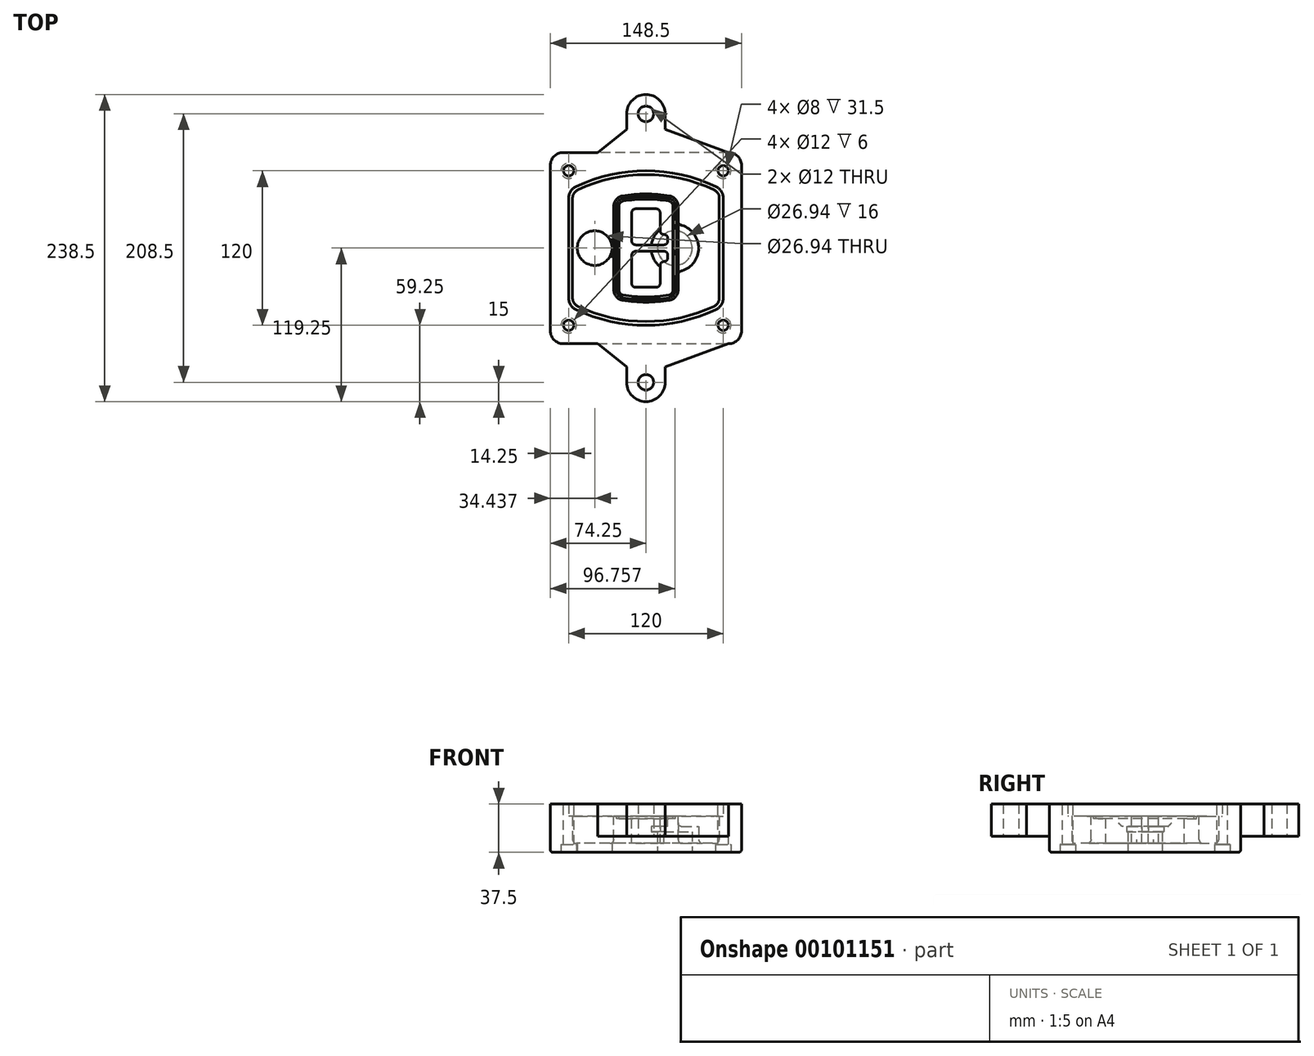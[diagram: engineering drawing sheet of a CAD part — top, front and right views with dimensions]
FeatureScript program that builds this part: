
annotation { "Feature Type Name" : "Feature", "Feature Type Description" : "" }
export const myFeature = defineFeature(function(context is Context, id is Id, definition is map)
    precondition{}
    {
        {
            var Q0;
            Q0=qCreatedBy(makeId("Top.planeOp"),FACE);
            var sketch = newSketch(context, id + "F0", { "sketchPlane" : qUnion([Q0])});
            skPoint(sketch, "E0.rect.middle", {"position": v(0, 0) * mm});
            skLineSegment(sketch, "E1.bottom", {"start": v(-64.25, -74.25) * mm, "end": v(64.25, -74.25) * mm});
            skLineSegment(sketch, "E1.top", {"start": v(-64.25, 74.25) * mm, "end": v(64.25, 74.25) * mm});
            skLineSegment(sketch, "E1.left", {"start": v(-74.25, -64.25) * mm, "end": v(-74.25, 64.25) * mm});
            skLineSegment(sketch, "E1.right", {"start": v(74.25, -64.25) * mm, "end": v(74.25, 64.25) * mm});
            skLineSegment(sketch, "E2", {"start": v(-74.25, 74.25) * mm, "end": v(74.25, -74.25) * mm, "construction": true});
            skLineSegment(sketch, "E3", {"start": v(74.25, 74.25) * mm, "end": v(-74.25, -74.25) * mm, "construction": true});
            skCircle(sketch, "E4", {"center": v(-60, 60) * mm, "radius": 4 * mm});
            skCircle(sketch, "E5", {"center": v(60, 60) * mm, "radius": 4 * mm});
            skCircle(sketch, "E6", {"center": v(60, -60) * mm, "radius": 4 * mm});
            skCircle(sketch, "E7", {"center": v(-60, -60) * mm, "radius": 4 * mm});
            skLineSegment(sketch, "E8", {"start": v(-60, 60) * mm, "end": v(60, 60) * mm, "construction": true});
            skLineSegment(sketch, "E9", {"start": v(60, 60) * mm, "end": v(60, -60) * mm, "construction": true});
            skLineSegment(sketch, "E10", {"start": v(60, -60) * mm, "end": v(-60, -60) * mm, "construction": true});
            skLineSegment(sketch, "E11", {"start": v(-60, -60) * mm, "end": v(-60, 60) * mm, "construction": true});
            skLineSegment(sketch, "E12", {"start": v(-60, 38.83) * mm, "end": v(-60, -38.83) * mm});
            skLineSegment(sketch, "E13", {"start": v(60, 38.83) * mm, "end": v(60, -38.83) * mm});
            skArc(sketch, "E14", {"start": v(54.26, 47.88) * mm, "mid": v(0, 60) * mm, "end": v(-54.26, 47.88) * mm});
            skArc(sketch, "E15", {"start": v(-54.26, -47.88) * mm, "mid": v(0, -60) * mm, "end": v(54.26, -47.88) * mm});
            skLineSegment(sketch, "E16", {"start": v(-60, 0) * mm, "end": v(60, 0) * mm, "construction": true});
            skPoint(sketch, "E17.visualSharp", {"position": v(-60, -45) * mm});
            skArc(sketch, "E17.filletArc", {"start": v(-60, -38.83) * mm, "mid": v(-58.44, -44.2) * mm, "end": v(-54.26, -47.88) * mm});
            skPoint(sketch, "E18.visualSharp", {"position": v(-60, 45) * mm});
            skArc(sketch, "E18.filletArc", {"start": v(-54.26, 47.88) * mm, "mid": v(-58.44, 44.2) * mm, "end": v(-60, 38.83) * mm});
            skPoint(sketch, "E19.visualSharp", {"position": v(60, 45) * mm});
            skArc(sketch, "E19.filletArc", {"start": v(60, 38.83) * mm, "mid": v(58.44, 44.2) * mm, "end": v(54.26, 47.88) * mm});
            skPoint(sketch, "E20.visualSharp", {"position": v(60, -45) * mm});
            skArc(sketch, "E20.filletArc", {"start": v(54.26, -47.88) * mm, "mid": v(58.44, -44.2) * mm, "end": v(60, -38.83) * mm});
            skPoint(sketch, "E21.visualSharp", {"position": v(-74.25, 74.25) * mm});
            skArc(sketch, "E21.filletArc", {"start": v(-64.25, 74.25) * mm, "mid": v(-71.32, 71.32) * mm, "end": v(-74.25, 64.25) * mm});
            skPoint(sketch, "E22.visualSharp", {"position": v(74.25, 74.25) * mm});
            skArc(sketch, "E22.filletArc", {"start": v(74.25, 64.25) * mm, "mid": v(71.32, 71.32) * mm, "end": v(64.25, 74.25) * mm});
            skPoint(sketch, "E23.visualSharp", {"position": v(74.25, -74.25) * mm});
            skArc(sketch, "E23.filletArc", {"start": v(64.25, -74.25) * mm, "mid": v(71.32, -71.32) * mm, "end": v(74.25, -64.25) * mm});
            skPoint(sketch, "E24.visualSharp", {"position": v(-74.25, -74.25) * mm});
            skArc(sketch, "E24.filletArc", {"start": v(-74.25, -64.25) * mm, "mid": v(-71.32, -71.32) * mm, "end": v(-64.25, -74.25) * mm});
            skArc(sketch, "E25.0", {"start": v(57, 38.83) * mm, "mid": v(55.9, 42.58) * mm, "end": v(52.98, 45.17) * mm});
            skLineSegment(sketch, "E25.1", {"start": v(57, 38.83) * mm, "end": v(57, -38.83) * mm});
            skArc(sketch, "E25.2", {"start": v(52.98, -45.17) * mm, "mid": v(55.9, -42.58) * mm, "end": v(57, -38.83) * mm});
            skArc(sketch, "E25.3", {"start": v(-52.98, -45.17) * mm, "mid": v(0, -57) * mm, "end": v(52.98, -45.17) * mm});
            skArc(sketch, "E25.4", {"start": v(-57, -38.83) * mm, "mid": v(-55.9, -42.58) * mm, "end": v(-52.98, -45.17) * mm});
            skArc(sketch, "E25.5", {"start": v(52.98, 45.17) * mm, "mid": v(0, 57) * mm, "end": v(-52.98, 45.17) * mm});
            skLineSegment(sketch, "E25.6", {"start": v(-57, 38.83) * mm, "end": v(-57, -38.83) * mm});
            skArc(sketch, "E25.7", {"start": v(-52.98, 45.17) * mm, "mid": v(-55.9, 42.58) * mm, "end": v(-57, 38.83) * mm});
            skArc(sketch, "E26.0", {"start": v(-55.96, 51.5) * mm, "mid": v(-61.82, 46.33) * mm, "end": v(-64, 38.83) * mm});
            skArc(sketch, "E26.1", {"start": v(55.96, 51.5) * mm, "mid": v(0, 64) * mm, "end": v(-55.96, 51.5) * mm});
            skArc(sketch, "E26.2", {"start": v(64, 38.83) * mm, "mid": v(61.82, 46.33) * mm, "end": v(55.96, 51.5) * mm});
            skLineSegment(sketch, "E26.3", {"start": v(64, 38.83) * mm, "end": v(64, -38.83) * mm});
            skArc(sketch, "E26.4", {"start": v(55.96, -51.5) * mm, "mid": v(61.82, -46.33) * mm, "end": v(64, -38.83) * mm});
            skLineSegment(sketch, "E26.5", {"start": v(-64, 38.83) * mm, "end": v(-64, -38.83) * mm});
            skArc(sketch, "E26.6", {"start": v(-55.96, -51.5) * mm, "mid": v(0, -64) * mm, "end": v(55.96, -51.5) * mm});
            skArc(sketch, "E26.7", {"start": v(-64, -38.83) * mm, "mid": v(-61.82, -46.33) * mm, "end": v(-55.96, -51.5) * mm});
            skSolve(sketch);
        }
        {
            var Q0;
            Q0=makeQuery(id+"F0.imprint","IMPRINT",FACE,{"disambiguationData":[TD([[makeQuery(id+"F0.imprint","IMPRINT",EDGE,{"derivedFrom":sQuery(id+"F0.wireOp",EDGE,"E1.bottom")}),1.0]])]});
            var Q1;
            Q1=makeQuery(id+"F0.imprint","IMPRINT",FACE,{"disambiguationData":[TD([[makeQuery(id+"F0.imprint","IMPRINT",EDGE,{"derivedFrom":sQuery(id+"F0.wireOp",EDGE,"E12")}),1.0]])]});
            var Q2;
            Q2=makeQuery(id+"F0.imprint","IMPRINT",FACE,{"disambiguationData":[TD([[makeQuery(id+"F0.imprint","IMPRINT",EDGE,{"derivedFrom":sQuery(id+"F0.wireOp",EDGE,"E25.0")}),1.0]])]});
            var Q3;
            Q3=makeQuery(id+"F0.imprint","IMPRINT",FACE,{"disambiguationData":[TD([[makeQuery(id+"F0.imprint","IMPRINT",EDGE,{"derivedFrom":sQuery(id+"F0.wireOp",EDGE,"E12")}),-1.0]])]});
            extrude(context, id + "F1", {"entities" : qUnion([Q0, Q1, Q2, Q3]), "oppositeDirection" : true, "depth" : 25 * mm});
        }
        {
            var Q0;
            Q0=makeQuery(id+"F0.imprint","IMPRINT",FACE,{"disambiguationData":[TD([[makeQuery(id+"F0.imprint","IMPRINT",EDGE,{"derivedFrom":sQuery(id+"F0.wireOp",EDGE,"E12")}),1.0]])]});
            extrude(context, id + "F2", {"entities" : qUnion([Q0]), "operationType" : NewBodyOperationType.ADD, "depth" : 3 * mm});
        }
        {
            var Q0;
            Q0=makeQuery(id+"F0.imprint","IMPRINT",FACE,{"disambiguationData":[TD([[makeQuery(id+"F0.imprint","IMPRINT",EDGE,{"derivedFrom":sQuery(id+"F0.wireOp",EDGE,"E25.0")}),1.0]])]});
            extrude(context, id + "F3", {"entities" : qUnion([Q0]), "operationType" : NewBodyOperationType.REMOVE, "oppositeDirection" : true, "depth" : 18 * mm});
        }
        {
            var Q0;
            Q0=makeQuery(id+"F2.opExtrude","CAP_FACE",FACE,{"disambiguationData":[OSD([sQuery(id+"F0.wireOp",EDGE,"E12"),sQuery(id+"F0.wireOp",EDGE,"E13"),sQuery(id+"F0.wireOp",EDGE,"E14"),sQuery(id+"F0.wireOp",EDGE,"E15"),sQuery(id+"F0.wireOp",EDGE,"E17.filletArc"),sQuery(id+"F0.wireOp",EDGE,"E18.filletArc"),sQuery(id+"F0.wireOp",EDGE,"E19.filletArc"),sQuery(id+"F0.wireOp",EDGE,"E20.filletArc"),sQuery(id+"F0.wireOp",EDGE,"E25.0"),sQuery(id+"F0.wireOp",EDGE,"E25.1"),sQuery(id+"F0.wireOp",EDGE,"E25.2"),sQuery(id+"F0.wireOp",EDGE,"E25.3"),sQuery(id+"F0.wireOp",EDGE,"E25.4"),sQuery(id+"F0.wireOp",EDGE,"E25.5"),sQuery(id+"F0.wireOp",EDGE,"E25.6"),sQuery(id+"F0.wireOp",EDGE,"E25.7")])],"isStart":false});
            var sketch = newSketch(context, id + "F4", { "sketchPlane" : qUnion([Q0])});
            skArc(sketch, "E27.0", {"start": v(-18.34, -40.45) * mm, "mid": v(0, -42) * mm, "end": v(18.34, -40.45) * mm});
            skArc(sketch, "E28.0", {"start": v(18.34, 40.45) * mm, "mid": v(0, 42) * mm, "end": v(-18.34, 40.45) * mm});
            skLineSegment(sketch, "E29", {"start": v(-25, 32.57) * mm, "end": v(-25, -32.57) * mm});
            skLineSegment(sketch, "E30", {"start": v(25, 32.57) * mm, "end": v(25, -32.57) * mm});
            skLineSegment(sketch, "E31", {"start": v(-25, 39.1) * mm, "end": v(25, 39.1) * mm, "construction": true});
            skLineSegment(sketch, "E32", {"start": v(-25, -39.1) * mm, "end": v(25, -39.1) * mm, "construction": true});
            skPoint(sketch, "E33.visualSharp", {"position": v(-25, 39.1) * mm});
            skArc(sketch, "E33.filletArc", {"start": v(-18.34, 40.45) * mm, "mid": v(-23.11, 37.73) * mm, "end": v(-25, 32.57) * mm});
            skPoint(sketch, "E34.visualSharp", {"position": v(25, 39.1) * mm});
            skArc(sketch, "E34.filletArc", {"start": v(25, 32.57) * mm, "mid": v(23.11, 37.73) * mm, "end": v(18.34, 40.45) * mm});
            skPoint(sketch, "E35.visualSharp", {"position": v(25, -39.1) * mm});
            skArc(sketch, "E35.filletArc", {"start": v(18.34, -40.45) * mm, "mid": v(23.11, -37.73) * mm, "end": v(25, -32.57) * mm});
            skPoint(sketch, "E36.visualSharp", {"position": v(-25, -39.1) * mm});
            skArc(sketch, "E36.filletArc", {"start": v(-25, -32.57) * mm, "mid": v(-23.11, -37.73) * mm, "end": v(-18.34, -40.45) * mm});
            skArc(sketch, "E37.0", {"start": v(52.98, 45.17) * mm, "mid": v(0, 57) * mm, "end": v(-52.98, 45.17) * mm});
            skArc(sketch, "E37.1", {"start": v(-52.98, 45.17) * mm, "mid": v(-55.9, 42.58) * mm, "end": v(-57, 38.83) * mm});
            skLineSegment(sketch, "E37.2", {"start": v(-57, 38.83) * mm, "end": v(-57, -38.83) * mm});
            skArc(sketch, "E37.3", {"start": v(-57, -38.83) * mm, "mid": v(-55.9, -42.58) * mm, "end": v(-52.98, -45.17) * mm});
            skArc(sketch, "E37.4", {"start": v(-52.98, -45.17) * mm, "mid": v(0, -57) * mm, "end": v(52.98, -45.17) * mm});
            skArc(sketch, "E37.5", {"start": v(52.98, -45.17) * mm, "mid": v(55.9, -42.58) * mm, "end": v(57, -38.83) * mm});
            skLineSegment(sketch, "E37.6", {"start": v(57, 38.83) * mm, "end": v(57, -38.83) * mm});
            skArc(sketch, "E37.7", {"start": v(57, 38.83) * mm, "mid": v(55.9, 42.58) * mm, "end": v(52.98, 45.17) * mm});
            skLineSegment(sketch, "E38.0", {"start": v(23, 32.57) * mm, "end": v(23, -32.57) * mm});
            skArc(sketch, "E38.1", {"start": v(18, -38.48) * mm, "mid": v(21.58, -36.44) * mm, "end": v(23, -32.57) * mm});
            skArc(sketch, "E38.2", {"start": v(-18, -38.48) * mm, "mid": v(0, -40) * mm, "end": v(18, -38.48) * mm});
            skArc(sketch, "E38.3", {"start": v(-23, -32.57) * mm, "mid": v(-21.58, -36.44) * mm, "end": v(-18, -38.48) * mm});
            skLineSegment(sketch, "E38.4", {"start": v(-23, 32.57) * mm, "end": v(-23, -32.57) * mm});
            skArc(sketch, "E38.5", {"start": v(23, 32.57) * mm, "mid": v(21.58, 36.44) * mm, "end": v(18, 38.48) * mm});
            skArc(sketch, "E38.6", {"start": v(-18, 38.48) * mm, "mid": v(-21.58, 36.44) * mm, "end": v(-23, 32.57) * mm});
            skArc(sketch, "E38.7", {"start": v(18, 38.48) * mm, "mid": v(0, 40) * mm, "end": v(-18, 38.48) * mm});
            skArc(sketch, "E39.0", {"start": v(21, 32.57) * mm, "mid": v(20.06, 35.15) * mm, "end": v(17.67, 36.5) * mm});
            skLineSegment(sketch, "E39.1", {"start": v(21, 32.57) * mm, "end": v(21, -32.57) * mm});
            skArc(sketch, "E39.2", {"start": v(17.67, -36.5) * mm, "mid": v(20.06, -35.15) * mm, "end": v(21, -32.57) * mm});
            skArc(sketch, "E39.3", {"start": v(-17.67, -36.5) * mm, "mid": v(0, -38) * mm, "end": v(17.67, -36.5) * mm});
            skArc(sketch, "E39.4", {"start": v(-21, -32.57) * mm, "mid": v(-20.06, -35.15) * mm, "end": v(-17.67, -36.5) * mm});
            skArc(sketch, "E39.5", {"start": v(17.67, 36.5) * mm, "mid": v(0, 38) * mm, "end": v(-17.67, 36.5) * mm});
            skLineSegment(sketch, "E39.6", {"start": v(-21, 32.57) * mm, "end": v(-21, -32.57) * mm});
            skArc(sketch, "E39.7", {"start": v(-17.67, 36.5) * mm, "mid": v(-20.06, 35.15) * mm, "end": v(-21, 32.57) * mm});
            skLineSegment(sketch, "E40", {"start": v(-25, 0) * mm, "end": v(25, 0) * mm, "construction": true});
            skLineSegment(sketch, "E41", {"start": v(-11, 5.5) * mm, "end": v(-11, 27.5) * mm});
            skLineSegment(sketch, "E42", {"start": v(-8, 30.5) * mm, "end": v(8, 30.5) * mm});
            skLineSegment(sketch, "E43", {"start": v(11, 27.5) * mm, "end": v(11, 13.5) * mm});
            skLineSegment(sketch, "E44", {"start": v(14, 10.5) * mm, "end": v(14, 10.5) * mm});
            skLineSegment(sketch, "E45", {"start": v(17, 7.5) * mm, "end": v(17, 5.5) * mm});
            skLineSegment(sketch, "E46", {"start": v(14, 2.5) * mm, "end": v(-8, 2.5) * mm});
            skPoint(sketch, "E47.visualSharp", {"position": v(-11, 30.5) * mm});
            skArc(sketch, "E47.filletArc", {"start": v(-8, 30.5) * mm, "mid": v(-10.12, 29.62) * mm, "end": v(-11, 27.5) * mm});
            skPoint(sketch, "E48.visualSharp", {"position": v(11, 30.5) * mm});
            skArc(sketch, "E48.filletArc", {"start": v(11, 27.5) * mm, "mid": v(10.12, 29.62) * mm, "end": v(8, 30.5) * mm});
            skPoint(sketch, "E49.visualSharp", {"position": v(11, 10.5) * mm});
            skArc(sketch, "E49.filletArc", {"start": v(11, 13.5) * mm, "mid": v(11.88, 11.38) * mm, "end": v(14, 10.5) * mm});
            skPoint(sketch, "E50.visualSharp", {"position": v(17, 10.5) * mm});
            skArc(sketch, "E50.filletArc", {"start": v(17, 7.5) * mm, "mid": v(16.12, 9.62) * mm, "end": v(14, 10.5) * mm});
            skPoint(sketch, "E51.visualSharp", {"position": v(17, 2.5) * mm});
            skArc(sketch, "E51.filletArc", {"start": v(14, 2.5) * mm, "mid": v(16.12, 3.38) * mm, "end": v(17, 5.5) * mm});
            skPoint(sketch, "E52.visualSharp", {"position": v(-11, 2.5) * mm});
            skArc(sketch, "E52.filletArc", {"start": v(-11, 5.5) * mm, "mid": v(-10.12, 3.38) * mm, "end": v(-8, 2.5) * mm});
            skLineSegment(sketch, "E53.0.MirrorCS", {"start": v(14, -2.5) * mm, "end": v(-8, -2.5) * mm});
            skArc(sketch, "E54.0.MirrorCS", {"start": v(-11, -5.5) * mm, "mid": v(-10.12, -3.38) * mm, "end": v(-8, -2.5) * mm});
            skLineSegment(sketch, "E55.0.MirrorCS", {"start": v(-11, -5.5) * mm, "end": v(-11, -27.5) * mm});
            skArc(sketch, "E56.0.MirrorCS", {"start": v(-8, -30.5) * mm, "mid": v(-10.12, -29.62) * mm, "end": v(-11, -27.5) * mm});
            skLineSegment(sketch, "E57.0.MirrorCS", {"start": v(-8, -30.5) * mm, "end": v(8, -30.5) * mm});
            skArc(sketch, "E58.0.MirrorCS", {"start": v(11, -27.5) * mm, "mid": v(10.12, -29.62) * mm, "end": v(8, -30.5) * mm});
            skLineSegment(sketch, "E59.0.MirrorCS", {"start": v(11, -27.5) * mm, "end": v(11, -13.5) * mm});
            skArc(sketch, "E60.0.MirrorCS", {"start": v(11, -13.5) * mm, "mid": v(11.88, -11.38) * mm, "end": v(14, -10.5) * mm});
            skArc(sketch, "E61.0.MirrorCS", {"start": v(17, -7.5) * mm, "mid": v(16.12, -9.62) * mm, "end": v(14, -10.5) * mm});
            skLineSegment(sketch, "E62.0.MirrorCS", {"start": v(17, -7.5) * mm, "end": v(17, -5.5) * mm});
            skArc(sketch, "E63.0.MirrorCS", {"start": v(14, -2.5) * mm, "mid": v(16.12, -3.38) * mm, "end": v(17, -5.5) * mm});
            skSolve(sketch);
        }
        {
            var Q0;
            Q0=makeQuery(id+"F4.imprint","IMPRINT",FACE,{"disambiguationData":[TD([[makeQuery(id+"F4.imprint","IMPRINT",EDGE,{"derivedFrom":sQuery(id+"F4.wireOp",EDGE,"E27.0")}),1.0]])]});
            var Q1;
            Q1=makeQuery(id+"F4.imprint","IMPRINT",FACE,{"disambiguationData":[TD([[makeQuery(id+"F4.imprint","IMPRINT",EDGE,{"derivedFrom":sQuery(id+"F4.wireOp",EDGE,"E38.0")}),-1.0]])]});
            var Q2;
            Q2=makeQuery(id+"F4.imprint","IMPRINT",FACE,{"disambiguationData":[TD([[makeQuery(id+"F4.imprint","IMPRINT",EDGE,{"derivedFrom":sQuery(id+"F4.wireOp",EDGE,"E39.0")}),1.0]])]});
            extrude(context, id + "F5", {"entities" : qUnion([Q0, Q1, Q2]), "operationType" : NewBodyOperationType.ADD, "endBound" : BoundingType.UP_TO_NEXT, "oppositeDirection" : true, "depth" : 25 * mm});
        }
        {
            var Q0;
            Q0=makeQuery(id+"F4.imprint","IMPRINT",FACE,{"disambiguationData":[TD([[makeQuery(id+"F4.imprint","IMPRINT",EDGE,{"derivedFrom":sQuery(id+"F4.wireOp",EDGE,"E38.0")}),-1.0]])]});
            extrude(context, id + "F6", {"entities" : qUnion([Q0]), "operationType" : NewBodyOperationType.REMOVE, "oppositeDirection" : true, "depth" : 2 * mm});
        }
        {
            var Q0;
            Q0=makeQuery(id+"F1.opExtrude","CAP_FACE",FACE,{"disambiguationData":[OSD([sQuery(id+"F0.wireOp",EDGE,"E1.bottom"),sQuery(id+"F0.wireOp",EDGE,"E1.top"),sQuery(id+"F0.wireOp",EDGE,"E1.left"),sQuery(id+"F0.wireOp",EDGE,"E1.right"),sQuery(id+"F0.wireOp",EDGE,"E4"),sQuery(id+"F0.wireOp",EDGE,"E5"),sQuery(id+"F0.wireOp",EDGE,"E6"),sQuery(id+"F0.wireOp",EDGE,"E7"),sQuery(id+"F0.wireOp",EDGE,"E21.filletArc"),sQuery(id+"F0.wireOp",EDGE,"E22.filletArc"),sQuery(id+"F0.wireOp",EDGE,"E23.filletArc"),sQuery(id+"F0.wireOp",EDGE,"E24.filletArc")])],"isStart":false});
            var sketch = newSketch(context, id + "F7", { "sketchPlane" : qUnion([Q0])});
            skCircle(sketch, "E64", {"center": v(22.5, 0) * mm, "radius": 13.47 * mm});
            skCircle(sketch, "E65", {"center": v(-39.81, 0) * mm, "radius": 13.47 * mm});
            skLineSegment(sketch, "E66", {"start": v(74.25, 0) * mm, "end": v(-74.25, 0) * mm});
            skCircle(sketch, "E67", {"center": v(22.5, 0) * mm, "radius": 18.47 * mm});
            skCircle(sketch, "E68", {"center": v(60, -60) * mm, "radius": 6 * mm});
            skCircle(sketch, "E69", {"center": v(-60, -60) * mm, "radius": 6 * mm});
            skCircle(sketch, "E70", {"center": v(-60, 60) * mm, "radius": 6 * mm});
            skCircle(sketch, "E71", {"center": v(60, 60) * mm, "radius": 6 * mm});
            skSolve(sketch);
        }
        {
            var Q0;
            {var subQ1=sQuery(id+"F7.wireOp",EDGE,"E66");var subQ4=sQuery(id+"F7.wireOp",EDGE,"E64");var subQ6=makeQuery(id+"F7.imprint","INTERSECT",VERTEX,{"disambiguationData":[OD(0.0)],"derivedFrom":[subQ4,subQ1]});Q0=makeQuery(id+"F7.imprint","IMPRINT",FACE,{"disambiguationData":[TD([[makeQuery(id+"F7.imprint","IMPRINT",EDGE,{"disambiguationData":[TD([[subQ6,-1.0]])],"derivedFrom":subQ4}),-1.0]])]});}
            var Q1;
            {var subQ0=sQuery(id+"F7.wireOp",EDGE,"E66");var subQ1=sQuery(id+"F7.wireOp",EDGE,"E64");var subQ3=makeQuery(id+"F7.imprint","INTERSECT",VERTEX,{"disambiguationData":[OD(0.0)],"derivedFrom":[subQ1,subQ0]});Q1=makeQuery(id+"F7.imprint","IMPRINT",FACE,{"disambiguationData":[TD([[makeQuery(id+"F7.imprint","IMPRINT",EDGE,{"disambiguationData":[TD([[subQ3,-1.0]])],"derivedFrom":subQ1}),1.0]])]});}
            var Q2;
            {var subQ0=sQuery(id+"F7.wireOp",EDGE,"E66");var subQ1=sQuery(id+"F7.wireOp",EDGE,"E64");var subQ3=makeQuery(id+"F7.imprint","INTERSECT",VERTEX,{"disambiguationData":[OD(0.0)],"derivedFrom":[subQ1,subQ0]});Q2=makeQuery(id+"F7.imprint","IMPRINT",FACE,{"disambiguationData":[TD([[makeQuery(id+"F7.imprint","IMPRINT",EDGE,{"disambiguationData":[TD([[subQ3,1.0]])],"derivedFrom":subQ1}),1.0]])]});}
            var Q3;
            {var subQ1=sQuery(id+"F7.wireOp",EDGE,"E66");var subQ4=sQuery(id+"F7.wireOp",EDGE,"E64");var subQ6=makeQuery(id+"F7.imprint","INTERSECT",VERTEX,{"disambiguationData":[OD(0.0)],"derivedFrom":[subQ4,subQ1]});Q3=makeQuery(id+"F7.imprint","IMPRINT",FACE,{"disambiguationData":[TD([[makeQuery(id+"F7.imprint","IMPRINT",EDGE,{"disambiguationData":[TD([[subQ6,1.0]])],"derivedFrom":subQ4}),-1.0]])]});}
            extrude(context, id + "F8", {"entities" : qUnion([Q0, Q1, Q2, Q3]), "operationType" : NewBodyOperationType.ADD, "oppositeDirection" : true, "depth" : 20 * mm});
        }
        {
            var Q0;
            {var subQ0=sQuery(id+"F7.wireOp",EDGE,"E66");var subQ1=sQuery(id+"F7.wireOp",EDGE,"E64");var subQ3=makeQuery(id+"F7.imprint","INTERSECT",VERTEX,{"disambiguationData":[OD(0.0)],"derivedFrom":[subQ1,subQ0]});Q0=makeQuery(id+"F7.imprint","IMPRINT",FACE,{"disambiguationData":[TD([[makeQuery(id+"F7.imprint","IMPRINT",EDGE,{"disambiguationData":[TD([[subQ3,-1.0]])],"derivedFrom":subQ1}),1.0]])]});}
            var Q1;
            {var subQ0=sQuery(id+"F7.wireOp",EDGE,"E66");var subQ1=sQuery(id+"F7.wireOp",EDGE,"E64");var subQ3=makeQuery(id+"F7.imprint","INTERSECT",VERTEX,{"disambiguationData":[OD(0.0)],"derivedFrom":[subQ1,subQ0]});Q1=makeQuery(id+"F7.imprint","IMPRINT",FACE,{"disambiguationData":[TD([[makeQuery(id+"F7.imprint","IMPRINT",EDGE,{"disambiguationData":[TD([[subQ3,1.0]])],"derivedFrom":subQ1}),1.0]])]});}
            extrude(context, id + "F9", {"entities" : qUnion([Q0, Q1]), "operationType" : NewBodyOperationType.REMOVE, "oppositeDirection" : true, "depth" : 16 * mm});
        }
        {
            var Q0;
            {var subQ0=sQuery(id+"F7.wireOp",EDGE,"E66");var subQ1=sQuery(id+"F7.wireOp",EDGE,"E65");var subQ3=makeQuery(id+"F7.imprint","INTERSECT",VERTEX,{"disambiguationData":[OD(0.0)],"derivedFrom":[subQ1,subQ0]});Q0=makeQuery(id+"F7.imprint","IMPRINT",FACE,{"disambiguationData":[TD([[makeQuery(id+"F7.imprint","IMPRINT",EDGE,{"disambiguationData":[TD([[subQ3,-1.0]])],"derivedFrom":subQ1}),1.0]])]});}
            var Q1;
            {var subQ0=sQuery(id+"F7.wireOp",EDGE,"E66");var subQ1=sQuery(id+"F7.wireOp",EDGE,"E65");var subQ3=makeQuery(id+"F7.imprint","INTERSECT",VERTEX,{"disambiguationData":[OD(0.0)],"derivedFrom":[subQ1,subQ0]});Q1=makeQuery(id+"F7.imprint","IMPRINT",FACE,{"disambiguationData":[TD([[makeQuery(id+"F7.imprint","IMPRINT",EDGE,{"disambiguationData":[TD([[subQ3,1.0]])],"derivedFrom":subQ1}),1.0]])]});}
            extrude(context, id + "F10", {"entities" : qUnion([Q0, Q1]), "operationType" : NewBodyOperationType.REMOVE, "oppositeDirection" : true, "depth" : 25 * mm});
        }
        {
            var Q0;
            Q0=makeQuery(id+"F7.imprint","IMPRINT",FACE,{"disambiguationData":[TD([[makeQuery(id+"F7.imprint","IMPRINT",EDGE,{"derivedFrom":sQuery(id+"F7.wireOp",EDGE,"E68")}),1.0]])]});
            var Q1;
            Q1=makeQuery(id+"F7.imprint","IMPRINT",FACE,{"disambiguationData":[TD([[makeQuery(id+"F7.imprint","IMPRINT",EDGE,{"derivedFrom":makeQuery(id+"F1.opExtrude","CAP_EDGE",EDGE,{"disambiguationData":[OSD([sQuery(id+"F0.wireOp",EDGE,"E5")])],"isStart":false})}),-1.0]])]});
            var Q2;
            Q2=makeQuery(id+"F7.imprint","IMPRINT",FACE,{"disambiguationData":[TD([[makeQuery(id+"F7.imprint","IMPRINT",EDGE,{"derivedFrom":sQuery(id+"F7.wireOp",EDGE,"E69")}),1.0]])]});
            var Q3;
            Q3=makeQuery(id+"F7.imprint","IMPRINT",FACE,{"disambiguationData":[TD([[makeQuery(id+"F7.imprint","IMPRINT",EDGE,{"derivedFrom":makeQuery(id+"F1.opExtrude","CAP_EDGE",EDGE,{"disambiguationData":[OSD([sQuery(id+"F0.wireOp",EDGE,"E4")])],"isStart":false})}),-1.0]])]});
            var Q4;
            Q4=makeQuery(id+"F7.imprint","IMPRINT",FACE,{"disambiguationData":[TD([[makeQuery(id+"F7.imprint","IMPRINT",EDGE,{"derivedFrom":sQuery(id+"F7.wireOp",EDGE,"E70")}),1.0]])]});
            var Q5;
            Q5=makeQuery(id+"F7.imprint","IMPRINT",FACE,{"disambiguationData":[TD([[makeQuery(id+"F7.imprint","IMPRINT",EDGE,{"derivedFrom":makeQuery(id+"F1.opExtrude","CAP_EDGE",EDGE,{"disambiguationData":[OSD([sQuery(id+"F0.wireOp",EDGE,"E7")])],"isStart":false})}),-1.0]])]});
            var Q6;
            Q6=makeQuery(id+"F7.imprint","IMPRINT",FACE,{"disambiguationData":[TD([[makeQuery(id+"F7.imprint","IMPRINT",EDGE,{"derivedFrom":sQuery(id+"F7.wireOp",EDGE,"E71")}),1.0]])]});
            var Q7;
            Q7=makeQuery(id+"F7.imprint","IMPRINT",FACE,{"disambiguationData":[TD([[makeQuery(id+"F7.imprint","IMPRINT",EDGE,{"derivedFrom":makeQuery(id+"F1.opExtrude","CAP_EDGE",EDGE,{"disambiguationData":[OSD([sQuery(id+"F0.wireOp",EDGE,"E6")])],"isStart":false})}),-1.0]])]});
            extrude(context, id + "F11", {"entities" : qUnion([Q0, Q1, Q2, Q3, Q4, Q5, Q6, Q7]), "operationType" : NewBodyOperationType.REMOVE, "oppositeDirection" : true, "depth" : 6 * mm});
        }
        {
            var Q0;
            Q0=makeQuery(id+"F9.boolean.opBoolean","COPY",FACE,{"derivedFrom":makeQuery(id+"F9.opExtrude","CAP_FACE",FACE,{"disambiguationData":[OSD([sQuery(id+"F7.wireOp",EDGE,"E64")])],"isStart":false})});
            var sketch = newSketch(context, id + "F12", { "sketchPlane" : qUnion([Q0])});
            skArc(sketch, "E72.0", {"start": v(11, 14.45) * mm, "mid": v(6.45, 9.13) * mm, "end": v(4.2, 2.5) * mm});
            skArc(sketch, "E72.1", {"start": v(4.2, -2.5) * mm, "mid": v(6.45, -9.13) * mm, "end": v(11, -14.45) * mm});
            skLineSegment(sketch, "E73", {"start": v(4.2, -2.5) * mm, "end": v(14, -2.5) * mm});
            skLineSegment(sketch, "E74.0", {"start": v(14, 2.5) * mm, "end": v(4.2, 2.5) * mm});
            skArc(sketch, "E74.1", {"start": v(14, 2.5) * mm, "mid": v(16.12, 3.38) * mm, "end": v(17, 5.5) * mm});
            skLineSegment(sketch, "E74.2", {"start": v(17, 7.5) * mm, "end": v(17, 5.5) * mm});
            skArc(sketch, "E74.3", {"start": v(17, 7.5) * mm, "mid": v(16.12, 9.62) * mm, "end": v(14, 10.5) * mm});
            skArc(sketch, "E74.4", {"start": v(11, 13.5) * mm, "mid": v(11.88, 11.38) * mm, "end": v(14, 10.5) * mm});
            skLineSegment(sketch, "E74.5", {"start": v(11, 14.45) * mm, "end": v(11, 13.5) * mm});
            skLineSegment(sketch, "E74.7", {"start": v(14, -2.5) * mm, "end": v(4.2, -2.5) * mm});
            skArc(sketch, "E74.8", {"start": v(14, -2.5) * mm, "mid": v(16.12, -3.38) * mm, "end": v(17, -5.5) * mm});
            skLineSegment(sketch, "E74.9", {"start": v(17, -7.5) * mm, "end": v(17, -5.5) * mm});
            skArc(sketch, "E74.10", {"start": v(17, -7.5) * mm, "mid": v(16.12, -9.62) * mm, "end": v(14, -10.5) * mm});
            skArc(sketch, "E74.11", {"start": v(11, -13.5) * mm, "mid": v(11.88, -11.38) * mm, "end": v(14, -10.5) * mm});
            skLineSegment(sketch, "E74.12", {"start": v(11, -14.45) * mm, "end": v(11, -13.5) * mm});
            skPoint(sketch, "E75.orphan", {"position": v(11, -27.5) * mm});
            skPoint(sketch, "E76.orphan", {"position": v(-8, -2.5) * mm});
            skPoint(sketch, "E77.orphan", {"position": v(-8, 2.5) * mm});
            skPoint(sketch, "E78.orphan", {"position": v(11, 27.5) * mm});
            skSolve(sketch);
        }
        {
            var Q0;
            {var subQ7=sQuery(id+"F12.wireOp",EDGE,"E72.0");var subQ14=sQuery(id+"F12.wireOp",EDGE,"E72.1");var subQ16=sQuery(id+"F12.wireOp",EDGE,"E74.1");var subQ18=sQuery(id+"F12.wireOp",EDGE,"E74.8");Q0=qUnion([makeQuery(id+"F12.imprint","IMPRINT",FACE,{"disambiguationData":[TD([[makeQuery(id+"F12.imprint","IMPRINT",EDGE,{"derivedFrom":subQ7}),1.0]])]}),makeQuery(id+"F12.imprint","IMPRINT",FACE,{"disambiguationData":[TD([[makeQuery(id+"F12.imprint","IMPRINT",EDGE,{"derivedFrom":subQ14}),1.0]])]}),makeQuery(id+"F12.imprint","IMPRINT",FACE,{"disambiguationData":[TD([[makeQuery(id+"F12.imprint","IMPRINT",EDGE,{"derivedFrom":subQ16}),1.0]])]}),makeQuery(id+"F12.imprint","IMPRINT",FACE,{"disambiguationData":[TD([[makeQuery(id+"F12.imprint","IMPRINT",EDGE,{"derivedFrom":subQ18}),-1.0]])]})]);}
            var Q1;
            Q1=makeQuery(id+"F5.boolean.opBoolean","SPLIT",FACE,{"disambiguationData":[TD([makeQuery(id+"F5.opExtrude","SWEPT_FACE",FACE,{"disambiguationData":[OSD([sQuery(id+"F4.wireOp",EDGE,"E41")])]})])],"derivedFrom":makeQuery(id+"F3.boolean.opBoolean","COPY",FACE,{"derivedFrom":makeQuery(id+"F3.opExtrude","CAP_FACE",FACE,{"disambiguationData":[OSD([sQuery(id+"F0.wireOp",EDGE,"E25.0"),sQuery(id+"F0.wireOp",EDGE,"E25.1"),sQuery(id+"F0.wireOp",EDGE,"E25.2"),sQuery(id+"F0.wireOp",EDGE,"E25.3"),sQuery(id+"F0.wireOp",EDGE,"E25.4"),sQuery(id+"F0.wireOp",EDGE,"E25.5"),sQuery(id+"F0.wireOp",EDGE,"E25.6"),sQuery(id+"F0.wireOp",EDGE,"E25.7")])],"isStart":false})})});
            extrude(context, id + "F13", {"entities" : qUnion([Q0]), "operationType" : NewBodyOperationType.REMOVE, "endBound" : BoundingType.UP_TO_SURFACE, "endBoundEntityFace" : qUnion([Q1]), "depth" : 25 * mm});
        }
        {
            var Q0;
            Q0=makeQuery(id+"F3.boolean.opBoolean","COPY",EDGE,{"derivedFrom":makeQuery(id+"F3.opExtrude","CAP_EDGE",EDGE,{"disambiguationData":[OSD([sQuery(id+"F0.wireOp",EDGE,"E25.6")])],"isStart":false})});
            var Q1;
            Q1=makeQuery(id+"F8.boolean.opBoolean","INTERSECT",EDGE,{"derivedFrom":[makeQuery(id+"F5.opExtrude","SWEPT_FACE",FACE,{"disambiguationData":[OSD([sQuery(id+"F4.wireOp",EDGE,"E30")])]}),makeQuery(id+"F8.opExtrude","CAP_FACE",FACE,{"disambiguationData":[OSD([sQuery(id+"F7.wireOp",EDGE,"E67")])],"isStart":false})]});
            var Q2;
            Q2=makeQuery(id+"F8.boolean.opBoolean","INTERSECT",EDGE,{"disambiguationData":[OD(1.0)],"derivedFrom":[makeQuery(id+"F5.opExtrude","SWEPT_FACE",FACE,{"disambiguationData":[OSD([sQuery(id+"F4.wireOp",EDGE,"E30")])]}),makeQuery(id+"F8.opExtrude","SWEPT_FACE",FACE,{"disambiguationData":[OSD([sQuery(id+"F7.wireOp",EDGE,"E67")])]})]});
            var Q3;
            {var subQ0=sQuery(id+"F4.wireOp",EDGE,"E30");Q3=makeQuery(id+"F8.boolean.opBoolean","SPLIT",EDGE,{"disambiguationData":[TD([makeQuery(id+"F5.opExtrude","SWEPT_FACE",FACE,{"disambiguationData":[OSD([sQuery(id+"F4.wireOp",EDGE,"E35.filletArc")])]})])],"derivedFrom":makeQuery(id+"F5.opExtrude","CAP_EDGE",EDGE,{"disambiguationData":[OSD([subQ0])],"isStart":false})});}
            var Q4;
            {var subQ0=sQuery(id+"F0.wireOp",EDGE,"E25.7");var subQ1=sQuery(id+"F0.wireOp",EDGE,"E25.1");var subQ2=sQuery(id+"F0.wireOp",EDGE,"E25.6");var subQ3=sQuery(id+"F0.wireOp",EDGE,"E25.5");var subQ4=sQuery(id+"F0.wireOp",EDGE,"E25.4");var subQ5=sQuery(id+"F0.wireOp",EDGE,"E25.0");var subQ6=sQuery(id+"F0.wireOp",EDGE,"E25.2");var subQ7=sQuery(id+"F0.wireOp",EDGE,"E25.3");Q4=makeQuery(id+"F8.boolean.opBoolean","INTERSECT",EDGE,{"derivedFrom":[makeQuery(id+"F5.boolean.opBoolean","SPLIT",FACE,{"disambiguationData":[TD([makeQuery(id+"F2.opExtrude","SWEPT_FACE",FACE,{"disambiguationData":[OSD([subQ5])]})])],"derivedFrom":makeQuery(id+"F3.boolean.opBoolean","COPY",FACE,{"derivedFrom":makeQuery(id+"F3.opExtrude","CAP_FACE",FACE,{"disambiguationData":[OSD([subQ5,subQ1,subQ6,subQ7,subQ4,subQ3,subQ2,subQ0])],"isStart":false})})}),makeQuery(id+"F8.opExtrude","SWEPT_FACE",FACE,{"disambiguationData":[OSD([sQuery(id+"F7.wireOp",EDGE,"E67")])]})]});}
            var Q5;
            Q5=makeQuery(id+"F8.boolean.opBoolean","INTERSECT",EDGE,{"disambiguationData":[OD(0.0)],"derivedFrom":[makeQuery(id+"F5.opExtrude","SWEPT_FACE",FACE,{"disambiguationData":[OSD([sQuery(id+"F4.wireOp",EDGE,"E30")])]}),makeQuery(id+"F8.opExtrude","SWEPT_FACE",FACE,{"disambiguationData":[OSD([sQuery(id+"F7.wireOp",EDGE,"E67")])]})]});
            fillet(context, id + "F14", {"entities" : qUnion([Q0, Q1, Q2, Q3, Q4, Q5]), "radius" : 3 * mm, "tangentPropagation" : true, "allowEdgeOverflow" : false});
        }
        {
            var Q0;
            Q0=makeQuery(id+"F1.opExtrude","CAP_EDGE",EDGE,{"disambiguationData":[OSD([sQuery(id+"F0.wireOp",EDGE,"E1.bottom")])],"isStart":false});
            fillet(context, id + "F15", {"entities" : qUnion([Q0]), "radius" : 2 * mm, "tangentPropagation" : true, "allowEdgeOverflow" : false});
        }
        {
            var Q0;
            {var subQ0=sQuery(id+"F0.wireOp",EDGE,"E22.filletArc");var subQ1=sQuery(id+"F0.wireOp",EDGE,"E7");var subQ2=sQuery(id+"F0.wireOp",EDGE,"E6");var subQ3=sQuery(id+"F0.wireOp",EDGE,"E5");var subQ4=sQuery(id+"F0.wireOp",EDGE,"E4");var subQ5=sQuery(id+"F0.wireOp",EDGE,"E1.bottom");var subQ6=sQuery(id+"F0.wireOp",EDGE,"E21.filletArc");var subQ7=sQuery(id+"F0.wireOp",EDGE,"E1.top");var subQ8=sQuery(id+"F0.wireOp",EDGE,"E1.left");var subQ9=sQuery(id+"F0.wireOp",EDGE,"E1.right");var subQ10=sQuery(id+"F0.wireOp",EDGE,"E23.filletArc");var subQ11=sQuery(id+"F0.wireOp",EDGE,"E24.filletArc");Q0=makeQuery(id+"F2.boolean.opBoolean","SPLIT",FACE,{"disambiguationData":[TD([makeQuery(id+"F1.opExtrude","SWEPT_FACE",FACE,{"disambiguationData":[OSD([subQ5])]})])],"derivedFrom":makeQuery(id+"F1.opExtrude","CAP_FACE",FACE,{"disambiguationData":[OSD([subQ5,subQ7,subQ8,subQ9,subQ4,subQ3,subQ2,subQ1,subQ6,subQ0,subQ10,subQ11])],"isStart":true})});}
            var sketch = newSketch(context, id + "F16", { "sketchPlane" : qUnion([Q0])});
            skLineSegment(sketch, "E79", {"start": v(0, 74.25) * mm, "end": v(0, 104.25) * mm, "construction": true});
            skLineSegment(sketch, "E80", {"start": v(-37.56, 74.25) * mm, "end": v(-15, 92.25) * mm});
            skLineSegment(sketch, "E81", {"start": v(-15, 92.25) * mm, "end": v(-15, 104.25) * mm});
            skLineSegment(sketch, "E82", {"start": v(15, 104.25) * mm, "end": v(15, 92.25) * mm});
            skLineSegment(sketch, "E83", {"start": v(15, 92.25) * mm, "end": v(64.25, 74.25) * mm});
            skArc(sketch, "E84", {"start": v(15, 104.25) * mm, "mid": v(0, 119.25) * mm, "end": v(-15, 104.25) * mm});
            skCircle(sketch, "E85", {"center": v(0, 104.25) * mm, "radius": 6 * mm});
            skLineSegment(sketch, "E86", {"start": v(-74.25, 0) * mm, "end": v(74.25, 0) * mm});
            skLineSegment(sketch, "E87.MirrorCS", {"start": v(-37.56, -74.25) * mm, "end": v(-15, -92.25) * mm});
            skLineSegment(sketch, "E88.MirrorCS", {"start": v(-15, -92.25) * mm, "end": v(-15, -104.25) * mm});
            skArc(sketch, "E89.MirrorCS", {"start": v(15, -104.25) * mm, "mid": v(0, -119.25) * mm, "end": v(-15, -104.25) * mm});
            skCircle(sketch, "E90.MirrorC", {"center": v(0, -104.25) * mm, "radius": 6 * mm});
            skLineSegment(sketch, "E91.MirrorCS", {"start": v(0, -74.25) * mm, "end": v(0, -104.25) * mm, "construction": true});
            skLineSegment(sketch, "E92.MirrorCS", {"start": v(15, -104.25) * mm, "end": v(15, -92.25) * mm});
            skLineSegment(sketch, "E93.MirrorCS", {"start": v(15, -92.25) * mm, "end": v(64.25, -74.25) * mm});
            skSolve(sketch);
        }
        {
            var Q0;
            {var subQ1=sQuery(id+"F16.wireOp",EDGE,"E80");Q0=makeQuery(id+"F16.imprint","IMPRINT",FACE,{"disambiguationData":[TD([[makeQuery(id+"F16.imprint","IMPRINT",EDGE,{"derivedFrom":subQ1}),-1.0]])]});}
            var Q1;
            Q1=makeQuery(id+"F16.imprint","IMPRINT",FACE,{"disambiguationData":[TD([[makeQuery(id+"F16.imprint","IMPRINT",EDGE,{"derivedFrom":makeQuery(id+"F1.opExtrude","CAP_EDGE",EDGE,{"disambiguationData":[OSD([sQuery(id+"F0.wireOp",EDGE,"E4")])],"isStart":true})}),-1.0]])]});
            var Q2;
            Q2=makeQuery(id+"F16.imprint","IMPRINT",FACE,{"disambiguationData":[TD([[makeQuery(id+"F16.imprint","IMPRINT",EDGE,{"derivedFrom":makeQuery(id+"F1.opExtrude","CAP_EDGE",EDGE,{"disambiguationData":[OSD([sQuery(id+"F0.wireOp",EDGE,"E6")])],"isStart":true})}),-1.0]])]});
            var Q3;
            {var subQ0=sQuery(id+"F16.wireOp",EDGE,"E87.MirrorCS");Q3=makeQuery(id+"F16.imprint","IMPRINT",FACE,{"disambiguationData":[TD([[makeQuery(id+"F16.imprint","IMPRINT",EDGE,{"derivedFrom":subQ0}),1.0]])]});}
            extrude(context, id + "F17", {"entities" : qUnion([Q0, Q1, Q2, Q3]), "operationType" : NewBodyOperationType.ADD, "endBound" : BoundingType.SYMMETRIC, "depth" : 25 * mm});
        }
    });
